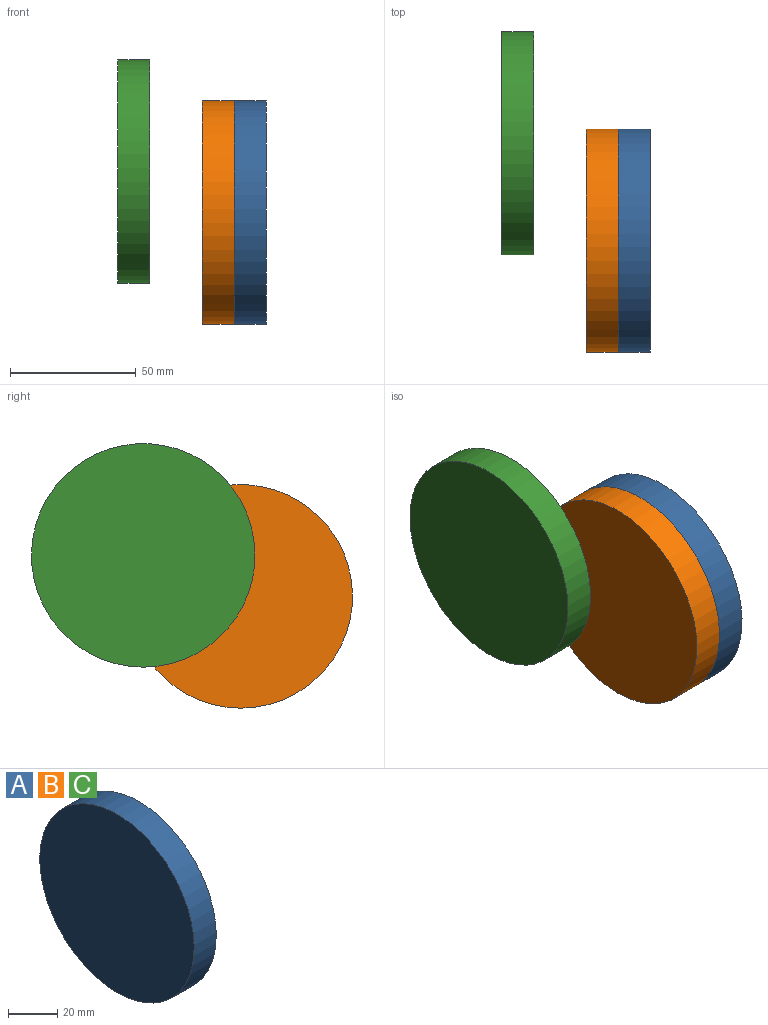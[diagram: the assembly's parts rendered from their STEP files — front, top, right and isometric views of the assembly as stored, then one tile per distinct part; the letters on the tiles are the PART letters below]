
ASSEMBLY  parts=3 mates=1
PART A: 3 faces, bbox 12.7x88.9x88.9 mm
  f0: cylinder r=44.45mm len=88.9mm, axis (-1,0,0), area 3547mm2, adj f1,f2
  f1: plane 88.9x88.9mm, normal (1,0,0), area 6207.2mm2, adj f0
  f2: plane 88.9x88.9mm, normal (-1,0,0), area 6207.2mm2, adj f0
PART B: same geometry as A
PART C: same geometry as A
PLACE A t=(46.43,-38.78,-16.31)mm
PLACE B t=(33.73,-38.78,-16.31)mm
PLACE C at identity
MATE fastened B.f0 <-> A.f0  axis (1,0,0) through (46.43,-38.78,-16.31)mm
